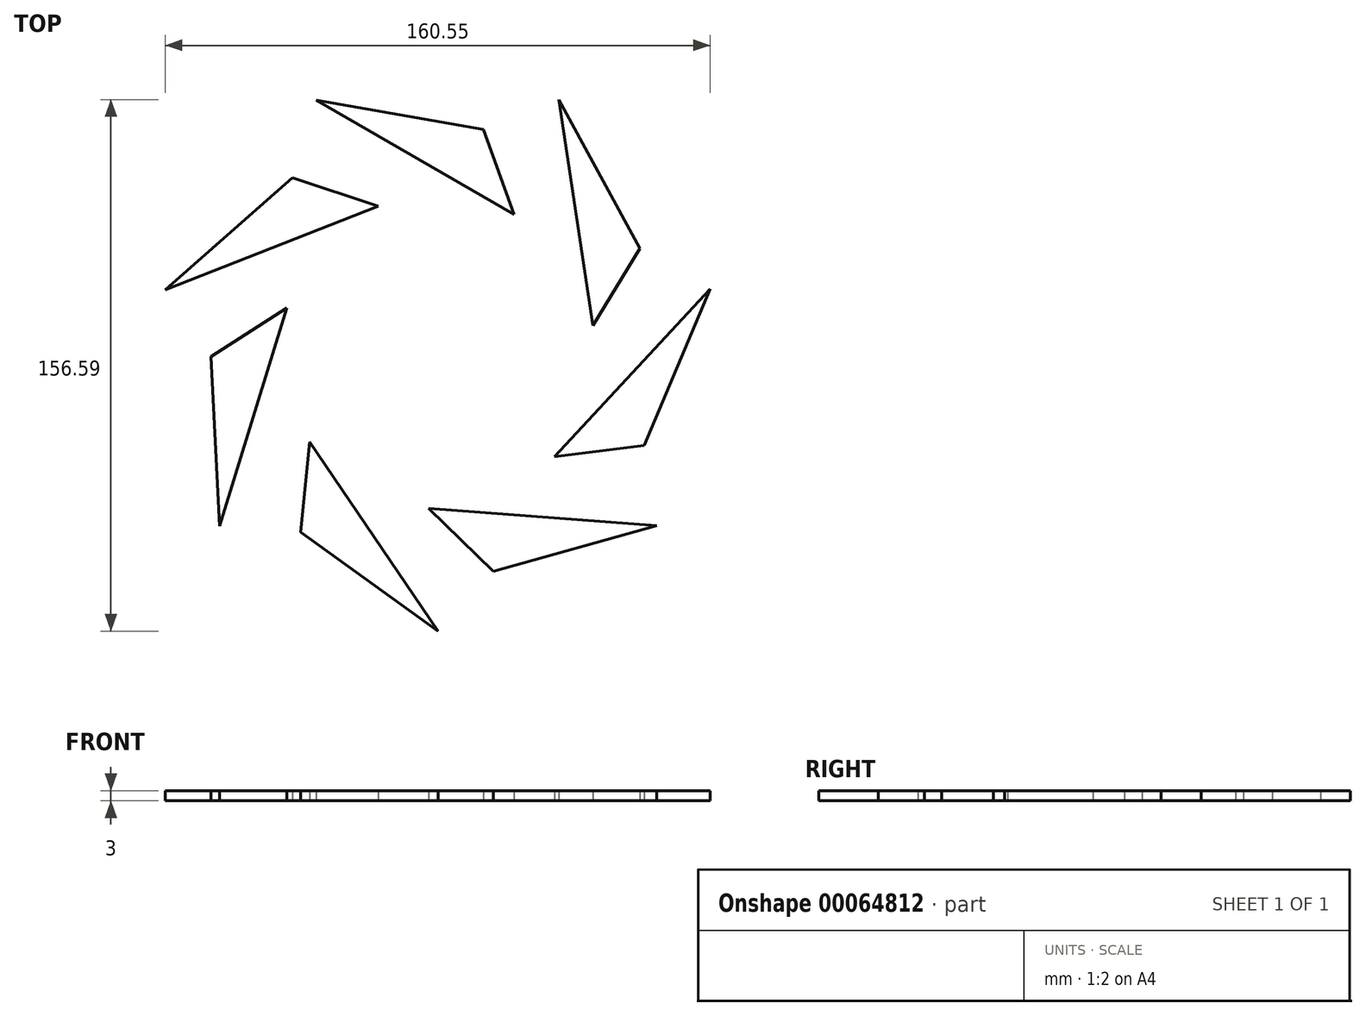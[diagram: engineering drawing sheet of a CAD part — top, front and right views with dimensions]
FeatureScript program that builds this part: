
annotation { "Feature Type Name" : "Feature", "Feature Type Description" : "" }
export const myFeature = defineFeature(function(context is Context, id is Id, definition is map)
    precondition{}
    {
        {
            var Q0;
            Q0=qCreatedBy(makeId("Top.planeOp"),FACE);
            var sketch = newSketch(context, id + "F0", { "sketchPlane" : qUnion([Q0])});
            skLineSegment(sketch, "E0", {"start": v(-35.86, 74.12) * mm, "end": v(13.38, 65.44) * mm});
            skLineSegment(sketch, "E1", {"start": v(13.38, 65.44) * mm, "end": v(22.48, 40.44) * mm});
            skLineSegment(sketch, "E2", {"start": v(22.48, 40.44) * mm, "end": v(-35.86, 74.12) * mm});
            skLineSegment(sketch, "E3", {"start": v(-35.86, 74.12) * mm, "end": v(17.93, 52.94) * mm, "construction": true});
            skLineSegment(sketch, "E4", {"start": v(22.48, 40.44) * mm, "end": v(-11.24, 69.78) * mm, "construction": true});
            skPoint(sketch, "E5", {"position": v(0, 60) * mm});
            skLineSegment(sketch, "E6.1.0", {"start": v(-17.6, 42.79) * mm, "end": v(-80.3, 18.18) * mm});
            skLineSegment(sketch, "E6.1.1", {"start": v(-42.82, 51.26) * mm, "end": v(-17.6, 42.79) * mm});
            skLineSegment(sketch, "E6.1.2", {"start": v(-80.3, 18.18) * mm, "end": v(-42.82, 51.26) * mm});
            skLineSegment(sketch, "E6.2.0", {"start": v(-44.43, 12.92) * mm, "end": v(-64.28, -51.45) * mm});
            skLineSegment(sketch, "E6.2.1", {"start": v(-66.78, -1.52) * mm, "end": v(-44.43, 12.92) * mm});
            skLineSegment(sketch, "E6.2.2", {"start": v(-64.28, -51.45) * mm, "end": v(-66.78, -1.52) * mm});
            skPoint(sketch, "E6.center", {"position": v(0, 0) * mm});
            skLineSegment(sketch, "E7", {"start": v(0, 0) * mm, "end": v(0, 60) * mm, "construction": true});
            skLineSegment(sketch, "E8.2.3.0", {"start": v(-37.8, -26.68) * mm, "end": v(0.15, -82.34) * mm});
            skLineSegment(sketch, "E8.3.3.0", {"start": v(-40.45, -53.15) * mm, "end": v(-37.8, -26.68) * mm});
            skLineSegment(sketch, "E8.6.3.0", {"start": v(0.15, -82.34) * mm, "end": v(-40.45, -53.15) * mm});
            skLineSegment(sketch, "E8.2.4.0", {"start": v(-2.7, -46.19) * mm, "end": v(64.47, -51.22) * mm});
            skLineSegment(sketch, "E8.3.4.0", {"start": v(16.34, -64.76) * mm, "end": v(-2.7, -46.19) * mm});
            skLineSegment(sketch, "E8.6.4.0", {"start": v(64.47, -51.22) * mm, "end": v(16.34, -64.76) * mm});
            skLineSegment(sketch, "E8.2.5.0", {"start": v(34.42, -30.91) * mm, "end": v(80.24, 18.47) * mm});
            skLineSegment(sketch, "E8.3.5.0", {"start": v(60.82, -27.6) * mm, "end": v(34.42, -30.91) * mm});
            skLineSegment(sketch, "E8.6.5.0", {"start": v(80.24, 18.47) * mm, "end": v(60.82, -27.6) * mm});
            skLineSegment(sketch, "E8.2.6.0", {"start": v(45.63, 7.64) * mm, "end": v(35.6, 74.25) * mm});
            skLineSegment(sketch, "E8.3.6.0", {"start": v(59.5, 30.34) * mm, "end": v(45.63, 7.64) * mm});
            skLineSegment(sketch, "E8.6.6.0", {"start": v(35.6, 74.25) * mm, "end": v(59.5, 30.34) * mm});
            skSolve(sketch);
        }
        {
            var Q0;
            Q0 = qSketchRegion(id + "F0", true);
            extrude(context, id + "F1", {"entities" : qUnion([Q0]), "depth" : 3 * mm});
        }
    });
